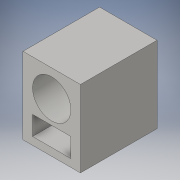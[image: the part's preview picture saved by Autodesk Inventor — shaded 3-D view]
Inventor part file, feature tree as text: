
AUTODESK INVENTOR PART (.ipt)
format: ipt  version: 2016 (Build 200138000, 138)  size: 115,200 bytes
history: native  units: in
note: dims shown in document units (in); Inventor stores cm internally (conversion verified against a paired STEP export)
features: extrude x3, sketch x3
ambient origin geometry x8: Origin, YZ Plane, XZ Plane, XY Plane, X Axis, Y Axis, Z Axis, Center Point
bodies: Solid1 (feature_tree)
feature tree (6):
  extrude  "Extrusion1"  Depth=1.0in
  extrude  "Extrusion2"  Depth=0.5in
  extrude  "Extrusion3"  Depth=0.5in
  sketch  "Sketch1"  dims[d0=0.75in d1=1.0in]
  sketch  "Sketch2"  dims[d2=1.0in d3=0.0in d4=0.5in]
  sketch  "Sketch3"  dims[d5=0.35in d6=0.5in d7=0.75in d8=0.25in d9=0.125in d10=0.125in d11=1.0in d12=0.0in d13=0.5in d14=0.125in d15=0.0in d16=0.1in]
